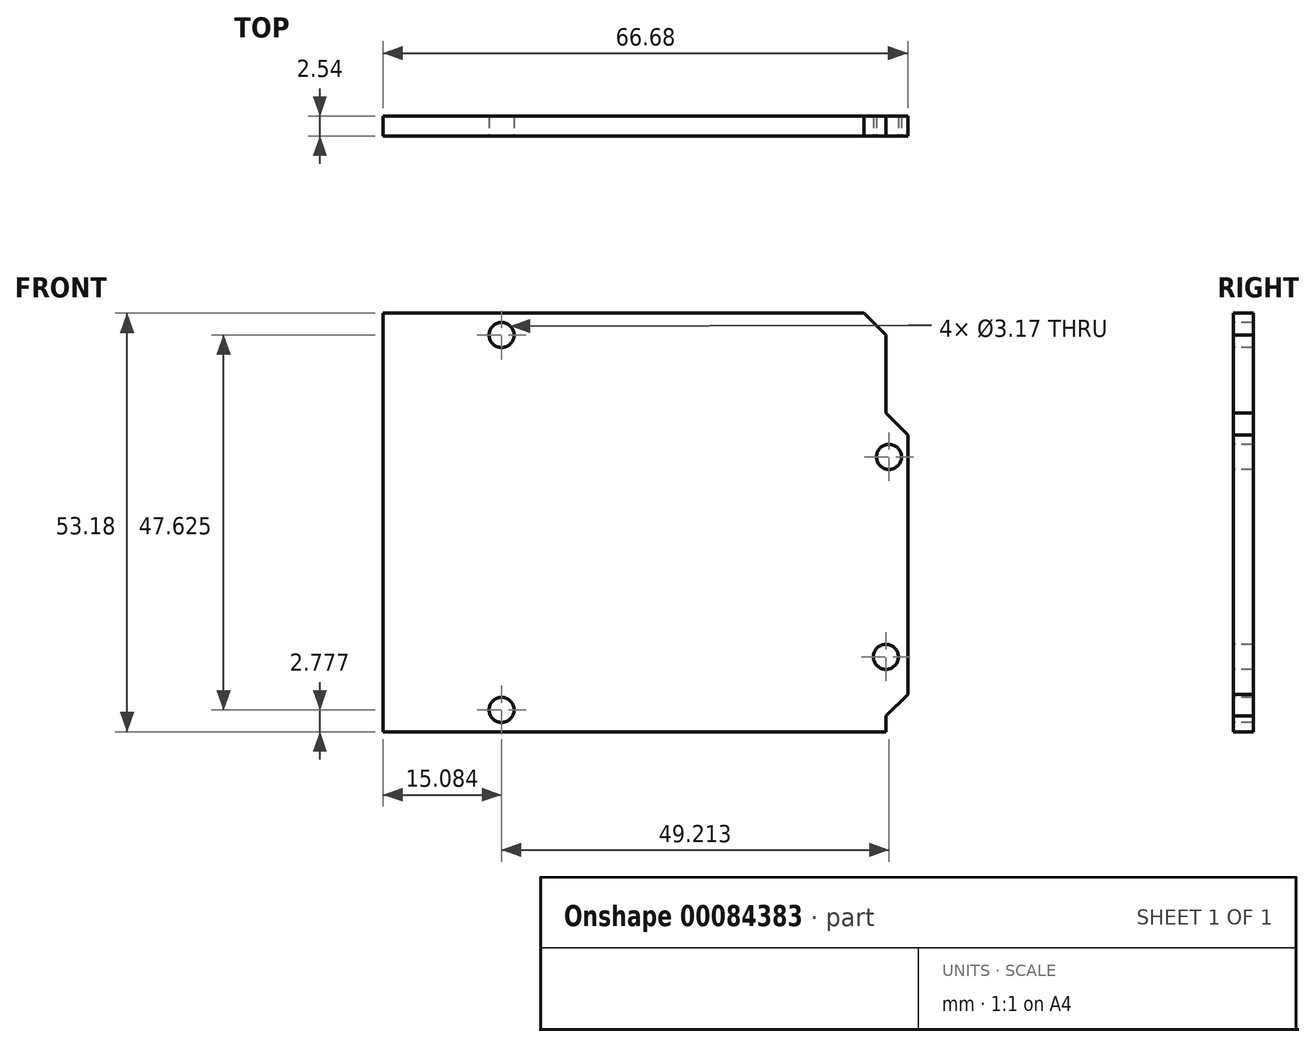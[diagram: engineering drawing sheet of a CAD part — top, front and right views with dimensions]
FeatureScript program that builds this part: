
annotation { "Feature Type Name" : "Feature", "Feature Type Description" : "" }
export const myFeature = defineFeature(function(context is Context, id is Id, definition is map)
    precondition{}
    {
        {
            var Q0;
            Q0=qCreatedBy(makeId("Front.planeOp"),FACE);
            var sketch = newSketch(context, id + "F0", { "sketchPlane" : qUnion([Q0])});
            skLineSegment(sketch, "E0.bottom", {"start": v(33.34, 26.6) * mm, "end": v(-33.34, 26.6) * mm});
            skLineSegment(sketch, "E0.top", {"start": v(33.34, -26.6) * mm, "end": v(-33.34, -26.6) * mm});
            skLineSegment(sketch, "E0.left", {"start": v(33.34, 26.6) * mm, "end": v(33.34, -26.6) * mm});
            skLineSegment(sketch, "E0.right", {"start": v(-33.34, 26.6) * mm, "end": v(-33.34, -26.6) * mm});
            skPoint(sketch, "E0.middle", {"position": v(0, 0) * mm});
            skSolve(sketch);
        }
        {
            var Q0;
            Q0=makeQuery(id+"F0.imprint","IMPRINT",FACE,{"disambiguationData":[TD([[makeQuery(id+"F0.imprint","IMPRINT",EDGE,{"derivedFrom":sQuery(id+"F0.wireOp",EDGE,"E0.bottom")}),1.0]])]});
            extrude(context, id + "F1", {"entities" : qUnion([Q0]), "depth" : 2.54 * mm});
        }
        {
            var Q0;
            Q0=makeQuery(id+"F1.opExtrude","CAP_FACE",FACE,{"disambiguationData":[OSD([sQuery(id+"F0.wireOp",EDGE,"E0.bottom"),sQuery(id+"F0.wireOp",EDGE,"E0.top"),sQuery(id+"F0.wireOp",EDGE,"E0.left"),sQuery(id+"F0.wireOp",EDGE,"E0.right")])],"isStart":false});
            var sketch = newSketch(context, id + "F2", { "sketchPlane" : qUnion([Q0])});
            skLineSegment(sketch, "E1", {"start": v(27.78, 26.6) * mm, "end": v(30.56, 23.81) * mm});
            skLineSegment(sketch, "E2", {"start": v(30.56, 23.81) * mm, "end": v(30.56, 13.9) * mm});
            skLineSegment(sketch, "E3", {"start": v(30.56, 13.9) * mm, "end": v(33.34, 11.11) * mm});
            skLineSegment(sketch, "E4", {"start": v(30.56, -26.6) * mm, "end": v(30.56, -24.6) * mm});
            skLineSegment(sketch, "E5", {"start": v(30.56, -24.6) * mm, "end": v(33.34, -21.83) * mm});
            skSolve(sketch);
        }
        {
            var Q0;
            Q0 = qSketchRegion(id + "F2", true);
            var Q1;
            {var subQ3=sQuery(id+"F2.wireOp",EDGE,"E1");Q1=makeQuery(id+"F2.imprint","IMPRINT",FACE,{"disambiguationData":[TD([[makeQuery(id+"F2.imprint","IMPRINT",EDGE,{"derivedFrom":subQ3}),1.0]])]});}
            var Q2;
            {var subQ0=sQuery(id+"F2.wireOp",EDGE,"E4");Q2=makeQuery(id+"F2.imprint","IMPRINT",FACE,{"disambiguationData":[TD([[makeQuery(id+"F2.imprint","IMPRINT",EDGE,{"derivedFrom":subQ0}),-1.0]])]});}
            extrude(context, id + "F3", {"entities" : qUnion([Q0, Q1, Q2]), "operationType" : NewBodyOperationType.REMOVE, "oppositeDirection" : true, "depth" : 25.4 * mm});
        }
        {
            var Q0;
            Q0=makeQuery(id+"F1.opExtrude","CAP_FACE",FACE,{"disambiguationData":[OSD([sQuery(id+"F0.wireOp",EDGE,"E0.bottom"),sQuery(id+"F0.wireOp",EDGE,"E0.top"),sQuery(id+"F0.wireOp",EDGE,"E0.left"),sQuery(id+"F0.wireOp",EDGE,"E0.right")])],"isStart":false});
            var sketch = newSketch(context, id + "F4", { "sketchPlane" : qUnion([Q0])});
            skCircle(sketch, "E6", {"center": v(30.96, 8.33) * mm, "radius": 1.59 * mm});
            skCircle(sketch, "E7", {"center": v(30.56, -17.07) * mm, "radius": 1.59 * mm});
            skCircle(sketch, "E8", {"center": v(-18.26, -23.81) * mm, "radius": 1.59 * mm});
            skCircle(sketch, "E9", {"center": v(-18.26, 23.81) * mm, "radius": 1.59 * mm});
            skSolve(sketch);
        }
        {
            var Q0;
            Q0 = qSketchRegion(id + "F4", true);
            extrude(context, id + "F5", {"entities" : qUnion([Q0]), "operationType" : NewBodyOperationType.REMOVE, "oppositeDirection" : true, "depth" : 25.4 * mm});
        }
    });
